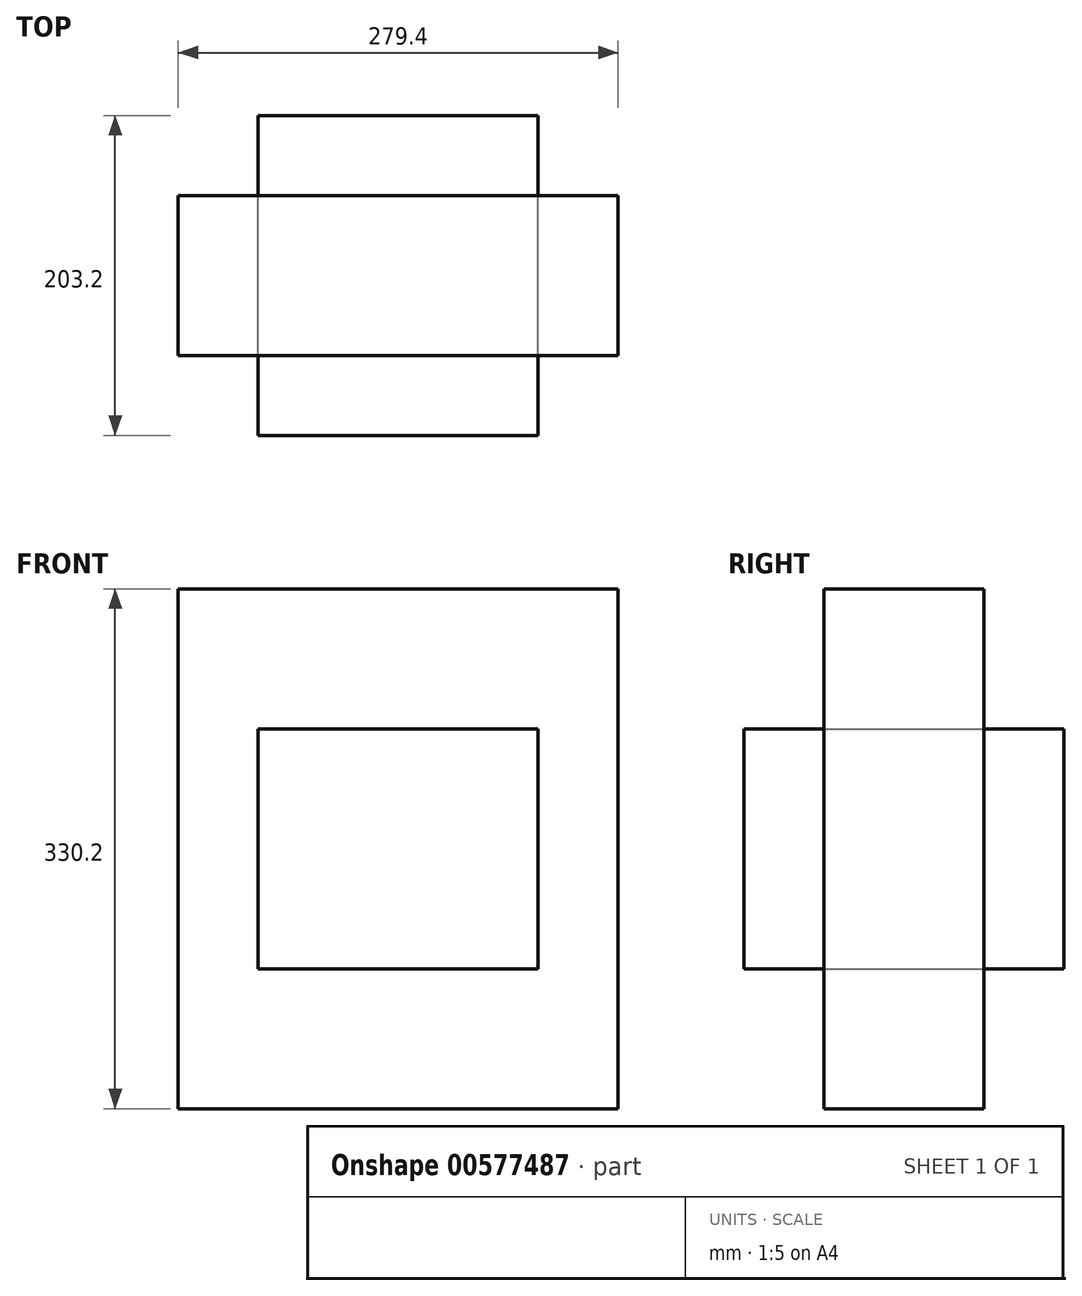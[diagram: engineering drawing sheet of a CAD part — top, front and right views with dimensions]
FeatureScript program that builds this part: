
annotation { "Feature Type Name" : "Feature", "Feature Type Description" : "" }
export const myFeature = defineFeature(function(context is Context, id is Id, definition is map)
    precondition{}
    {
        {
            var Q0;
            Q0=qCreatedBy(makeId("Front.planeOp"),FACE);
            var sketch = newSketch(context, id + "F0", { "sketchPlane" : qUnion([Q0])});
            skLineSegment(sketch, "E0.bottom", {"start": v(-139.7, 165.1) * mm, "end": v(139.7, 165.1) * mm});
            skLineSegment(sketch, "E0.top", {"start": v(-139.7, -165.1) * mm, "end": v(139.7, -165.1) * mm});
            skLineSegment(sketch, "E0.left", {"start": v(-139.7, 165.1) * mm, "end": v(-139.7, -165.1) * mm});
            skLineSegment(sketch, "E0.right", {"start": v(139.7, 165.1) * mm, "end": v(139.7, -165.1) * mm});
            skSolve(sketch);
        }
        {
            var Q0;
            Q0=makeQuery(id+"F0.imprint","IMPRINT",FACE,{"disambiguationData":[TD([[makeQuery(id+"F0.imprint","IMPRINT",EDGE,{"derivedFrom":sQuery(id+"F0.wireOp",EDGE,"E0.bottom")}),-1.0]])]});
            extrude(context, id + "F1", {"entities" : qUnion([Q0]), "endBound" : BoundingType.SYMMETRIC, "depth" : 101.6 * mm, "offsetDistance" : 25.4 * mm});
        }
        {
            var Q0;
            Q0=qCreatedBy(makeId("Front.planeOp"),FACE);
            var sketch = newSketch(context, id + "F2", { "sketchPlane" : qUnion([Q0])});
            skLineSegment(sketch, "E1.bottom", {"start": v(-88.9, 76.2) * mm, "end": v(88.9, 76.2) * mm});
            skLineSegment(sketch, "E1.top", {"start": v(-88.9, -76.2) * mm, "end": v(88.9, -76.2) * mm});
            skLineSegment(sketch, "E1.left", {"start": v(-88.9, 76.2) * mm, "end": v(-88.9, -76.2) * mm});
            skLineSegment(sketch, "E1.right", {"start": v(88.9, 76.2) * mm, "end": v(88.9, -76.2) * mm});
            skSolve(sketch);
        }
        {
            var Q0;
            Q0=makeQuery(id+"F2.imprint","IMPRINT",FACE,{"disambiguationData":[TD([[makeQuery(id+"F2.imprint","IMPRINT",EDGE,{"derivedFrom":sQuery(id+"F2.wireOp",EDGE,"E1.bottom")}),-1.0]])]});
            extrude(context, id + "F3", {"entities" : qUnion([Q0]), "endBound" : BoundingType.SYMMETRIC, "depth" : 203.2 * mm, "offsetDistance" : 25.4 * mm});
        }
    });
